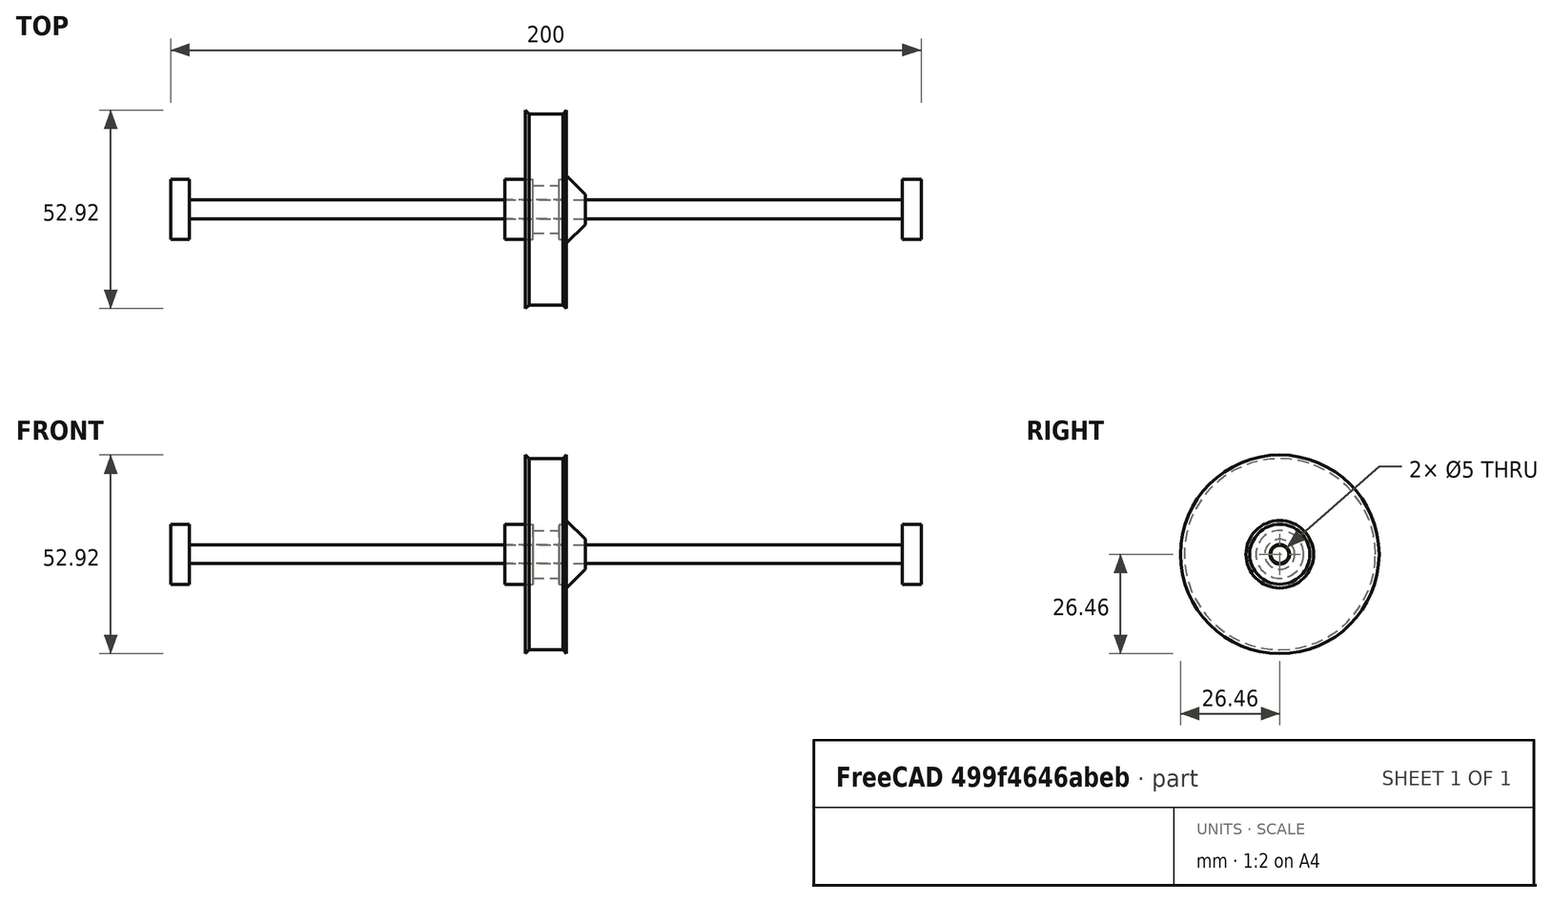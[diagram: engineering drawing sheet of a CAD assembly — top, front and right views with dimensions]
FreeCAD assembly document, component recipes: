
FREECAD ASSEMBLY — COMPONENT RECIPES ("miniXY-ZDrive")

This assembly document has 3 components, labeled P0..P2 below (a component is one placed body or linked part). 3 of them carry a construction recipe — the FreeCAD feature program that regenerates the part from scratch, quoted from this document or its linked companion documents; the rest are supplied as boundary geometry only. No exploded tour is included for this assembly.
COMPONENT P0 — recipe-attached ("DriveShaft", modeled in this document).
Construction recipe (the document's own serialized feature program — sketch geometry with constraints, then the solid features built on it; lengths are millimeters unless a unit is written):

FEATURE [Sketcher::SketchObject] Sketch119
  FullyConstrained = true
  MapMode = 5
  Support = -> [XY_Plane002]
  expr: Constraints[13] = <<Variables>>.DriveShaftLength
  sketch-geometry (16):
    g0: LineSegment StartX=-100 StartY=-8 StartZ=0 EndX=-95 EndY=-8 EndZ=0
    g1: LineSegment StartX=-95 StartY=-8 StartZ=0 EndX=-95 EndY=-2.5 EndZ=0
    g2: LineSegment StartX=-95 StartY=-2.5 StartZ=0 EndX=95 EndY=-2.5 EndZ=0
    g3: LineSegment StartX=95 StartY=-2.5 StartZ=0 EndX=95 EndY=-8 EndZ=0
    g4: LineSegment StartX=95 StartY=-8 StartZ=0 EndX=100 EndY=-8 EndZ=0
    g5: LineSegment StartX=100 StartY=0 StartZ=0 EndX=-100 EndY=0 EndZ=0
    g6: LineSegment StartX=-100 StartY=-3.5 StartZ=0 EndX=100 EndY=-3.5 EndZ=0
    g7: LineSegment StartX=-100 StartY=-7 StartZ=0 EndX=100 EndY=-7 EndZ=0
    g8: LineSegment StartX=-100 StartY=0 StartZ=0 EndX=-100 EndY=-2.4 EndZ=0
    g9: LineSegment StartX=-100 StartY=-2.4 StartZ=0 EndX=-99.9 EndY=-2.5 EndZ=0
    g10: LineSegment StartX=-99.9 StartY=-2.5 StartZ=0 EndX=-100 EndY=-2.6 EndZ=0
    g11: LineSegment StartX=99.9 StartY=-2.5 StartZ=0 EndX=100 EndY=-2.4 EndZ=0
    g12: LineSegment StartX=100 StartY=-2.4 StartZ=0 EndX=100 EndY=0 EndZ=0
    g13: LineSegment StartX=100 StartY=-8 StartZ=0 EndX=100 EndY=-2.6 EndZ=0
    g14: LineSegment StartX=100 StartY=-2.6 StartZ=0 EndX=99.9 EndY=-2.5 EndZ=0
    g15: LineSegment StartX=-100 StartY=-2.6 StartZ=0 EndX=-100 EndY=-8 EndZ=0
  constraints (40):
    c: Coincident(g0,g1)
    c: Vertical(g1)
    c: Coincident(g1,g2)
    c: Coincident(g2,g3)
    c: Coincident(g3,g4)
    c: Coincident(g4,g13)
    c: Coincident(g12,g5)
    c: Horizontal(g0)
    c: Symmetric(g5,g12,g-2)
    c: Symmetric(g1,g2,g-2)
    c: Symmetric(g0,g3,g-2)
    c: Symmetric(g0,g4,g-2)
    c: PointOnObject(g5,g-1)
    c: DistanceX(g5,g5) = 200
    c: DistanceY(g0) = -8
    c: DistanceY(g1) = -2.5
    c: DistanceX(g0,g0) = 5
    c: Coincident(g8,g5)
    c: Symmetric(g6,g6,g-2)
    c: Symmetric(g7,g7,g-2)
    c: DistanceY(g6,g1) = 1
    c: Coincident(g9,g10)
    c: Coincident(g8,g9)
    c: Vertical(g8)
    c: Coincident(g10,g15)
    c: PointOnObject(g9,g2)
    c: Symmetric(g8,g10,g2)
    c: Angle(g9) = -0.785398
    c: DistanceY(g10,g8) = 0.2
    c: DistanceY(g0,g7) = 1
    c: Coincident(g14,g11)
    c: Coincident(g11,g12)
    c: Coincident(g13,g14)
    c: Symmetric(g11,g9,g-2)
    c: Symmetric(g8,g11,g-2)
    c: Symmetric(g13,g10,g-2)
    c: Vertical(g15)
    c: PointOnObject(g6,g8)
    c: PointOnObject(g7,g8)
    c: Coincident(g15,g0)
FEATURE [PartDesign::Revolution] Revolution002
  Angle = 360
  Axis = (1,0,0)
  Base = (0,0,0)
  Profile = -> Sketch119
  ReferenceAxis = -> Sketch119 [H_Axis]
  Reversed = true
FEATURE [PartDesign::Body] Body  label="ShaftBody"
  Group = -> [Sketch119,Revolution002]
  Origin = -> Origin002
  Tip = -> Revolution002
COMPONENT P1 — recipe-attached ("Pully80T", modeled in this document).
Construction recipe (the document's own serialized feature program — sketch geometry with constraints, then the solid features built on it; lengths are millimeters unless a unit is written):

FEATURE [Sketcher::SketchObject] Sketch
  FullyConstrained = true
  MapMode = 5
  Support = -> [XY_Plane004]
  expr: Constraints[21] = -50.93 / 2
  sketch-geometry (10):
    g0: LineSegment StartX=-11 StartY=-2.5 StartZ=0 EndX=-11 EndY=-8 EndZ=0
    g1: LineSegment StartX=-11 StartY=-8 StartZ=0 EndX=-5.5 EndY=-8 EndZ=0
    g2: LineSegment StartX=-5.5 StartY=-8 StartZ=0 EndX=-5.5 EndY=-26.465 EndZ=0
    g3: LineSegment StartX=-5.5 StartY=-26.465 StartZ=0 EndX=-4.5 EndY=-25.465 EndZ=0
    g4: LineSegment StartX=-4.5 StartY=-25.465 StartZ=0 EndX=4.5 EndY=-25.465 EndZ=0
    g5: LineSegment StartX=4.5 StartY=-25.465 StartZ=0 EndX=5.5 EndY=-26.465 EndZ=0
    g6: LineSegment StartX=5.5 StartY=-26.465 StartZ=0 EndX=5.5 EndY=-9 EndZ=0
    g7: LineSegment StartX=5.5 StartY=-9 StartZ=0 EndX=10.5 EndY=-4 EndZ=0
    g8: LineSegment StartX=10.5 StartY=-4 StartZ=0 EndX=10.5 EndY=-2.5 EndZ=0
    g9: LineSegment StartX=10.5 StartY=-2.5 StartZ=0 EndX=-11 EndY=-2.5 EndZ=0
  constraints (28):
    c: Vertical(g0)
    c: Coincident(g0,g1)
    c: Coincident(g1,g2)
    c: Vertical(g2)
    c: Coincident(g2,g3)
    c: Coincident(g3,g4)
    c: Coincident(g4,g5)
    c: Coincident(g5,g6)
    c: Coincident(g6,g7)
    c: Coincident(g7,g8)
    c: Coincident(g8,g9)
    c: Coincident(g9,g0)
    c: Horizontal(g9)
    c: Angle(g3) = 0.785398
    c: Parallel(g3,g7)
    c: Vertical(g6)
    c: Vertical(g8)
    c: Symmetric(g3,g4,g-2)
    c: DistanceX(g4,g4) = 9
    c: Symmetric(g2,g5,g-2)
    c: DistanceX(g2,g3) = 1
    c: DistanceY(g3) = -25.465
    c: Horizontal(g1)
    c: DistanceY(g0) = -2.5
    c: DistanceX(g1,g1) = 5.5
    c: DistanceY(g0) = -8
    c: DistanceX(g7,g7) = 5
    c: DistanceY(g8,g8) = 1.5
FEATURE [PartDesign::Revolution] Revolution
  Angle = 360
  Axis = (1,0,0)
  Base = (0,0,0)
  Profile = -> Sketch
  ReferenceAxis = -> Sketch [H_Axis]
  Reversed = true
FEATURE [PartDesign::Body] Body002  label="Pully80TBody"
  Group = -> [Sketch,Revolution]
  Origin = -> Origin004
  Tip = -> Revolution
COMPONENT P2 — recipe-attached ("PullyDrive", modeled in this document).
Construction recipe (the document's own serialized feature program — sketch geometry with constraints, then the solid features built on it; lengths are millimeters unless a unit is written):

FEATURE [Sketcher::SketchObject] Sketch118
  FullyConstrained = true
  MapMode = 5
  Support = -> [XY_Plane003]
  expr: Constraints[18] = -<<Variables>>.PullyDriveDiameter / 2
  sketch-geometry (8):
    g0: LineSegment StartX=-11 StartY=-2.5 StartZ=0 EndX=-11 EndY=-8 EndZ=0
    g1: LineSegment StartX=-11 StartY=-8 StartZ=0 EndX=-3.5 EndY=-8 EndZ=0
    g2: LineSegment StartX=-3.5 StartY=-8 StartZ=0 EndX=-3.5 EndY=-6.365 EndZ=0
    g3: LineSegment StartX=-3.5 StartY=-6.365 StartZ=0 EndX=3.5 EndY=-6.365 EndZ=0
    g4: LineSegment StartX=3.5 StartY=-6.365 StartZ=0 EndX=3.5 EndY=-8 EndZ=0
    g5: LineSegment StartX=3.5 StartY=-8 StartZ=0 EndX=5 EndY=-8 EndZ=0
    g6: LineSegment StartX=5 StartY=-8 StartZ=0 EndX=5 EndY=-2.5 EndZ=0
    g7: LineSegment StartX=5 StartY=-2.5 StartZ=0 EndX=-11 EndY=-2.5 EndZ=0
  constraints (23):
    c: Vertical(g0)
    c: Coincident(g0,g1)
    c: Horizontal(g1)
    c: Coincident(g1,g2)
    c: Coincident(g2,g3)
    c: Coincident(g3,g4)
    c: Vertical(g4)
    c: Coincident(g4,g5)
    c: Coincident(g5,g6)
    c: Vertical(g6)
    c: Coincident(g6,g7)
    c: Coincident(g7,g0)
    c: Horizontal(g7)
    c: Symmetric(g2,g3,g-2)
    c: Vertical(g2)
    c: DistanceX(g7,g7) = 16
    c: DistanceY(g0) = -2.5
    c: DistanceY(g0) = -8
    c: DistanceY(g2) = -6.365
    c: DistanceX(g5,g5) = 1.5
    c: DistanceX(g1,g1) = 7.5
    c: Horizontal(g5)
    c: DistanceY(g5) = -8
FEATURE [PartDesign::Revolution] Revolution001
  Angle = 360
  Axis = (1,0,0)
  Base = (0,0,0)
  Profile = -> Sketch118
  ReferenceAxis = -> Sketch118 [H_Axis]
  Reversed = true
FEATURE [PartDesign::Body] Body001  label="PullyDriveBody"
  Group = -> [Sketch118,Revolution001]
  Origin = -> Origin003
  Tip = -> Revolution001
PROVENANCE & LICENSES
A FreeCAD (.FCStd) document from a public repository crawl; recipes are the document's own serialized feature recipes (and, for linked parts, companion documents' recipes).
License: gpl-3.0.
